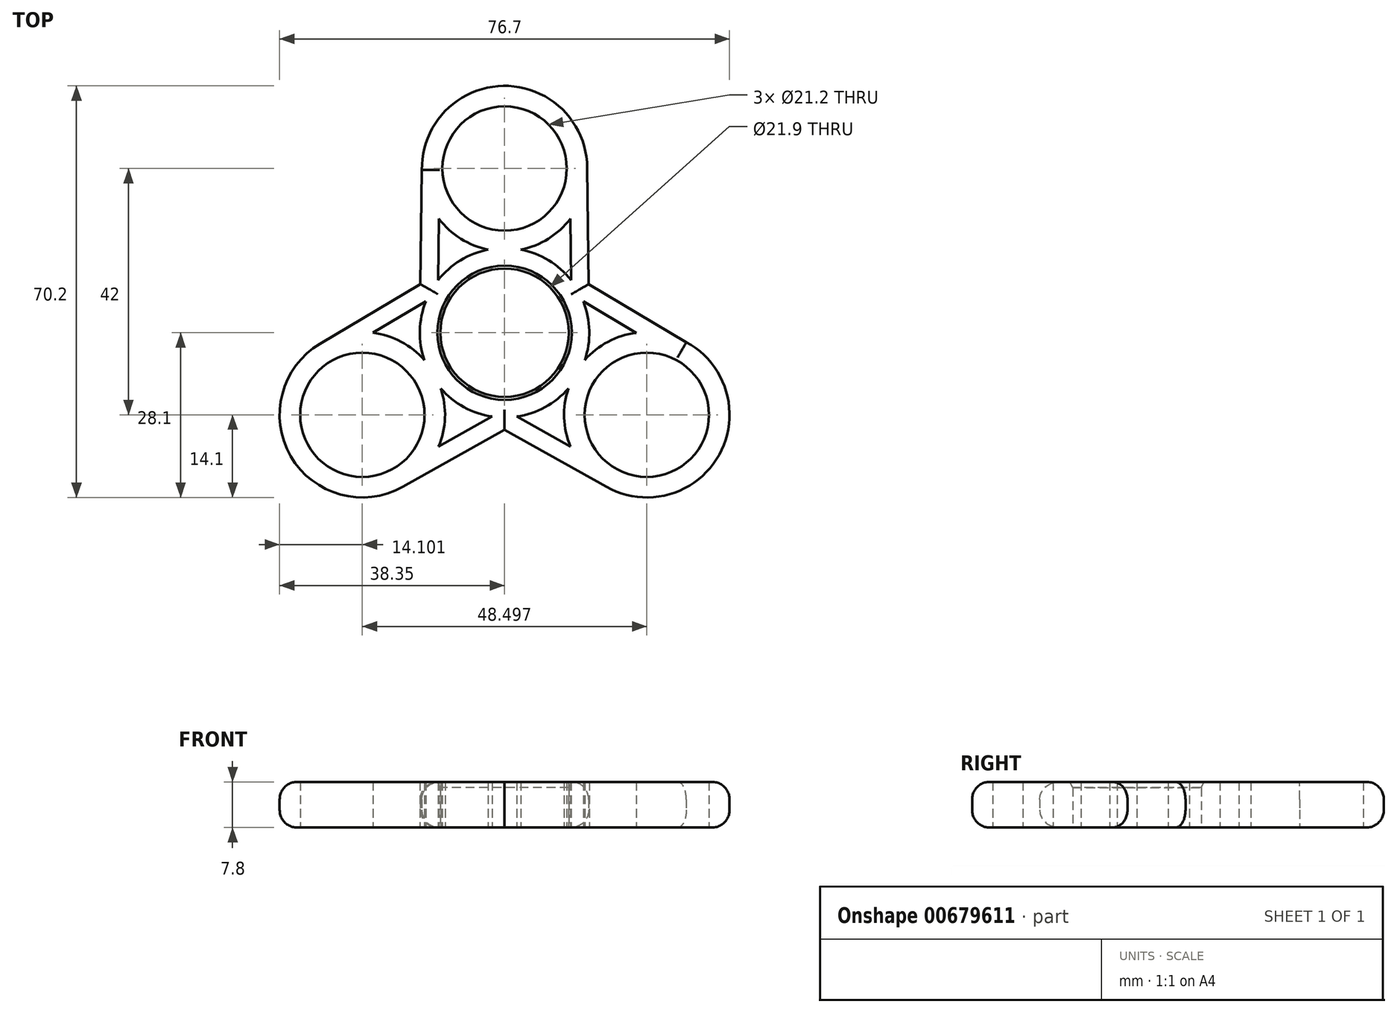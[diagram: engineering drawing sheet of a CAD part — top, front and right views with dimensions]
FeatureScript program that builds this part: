
annotation { "Feature Type Name" : "Feature", "Feature Type Description" : "" }
export const myFeature = defineFeature(function(context is Context, id is Id, definition is map)
    precondition{}
    {
        {
            var Q0;
            Q0=qCreatedBy(makeId("Top.planeOp"),FACE);
            var sketch = newSketch(context, id + "F0", { "sketchPlane" : qUnion([Q0])});
            skCircle(sketch, "E0", {"center": v(0, 0) * mm, "radius": 10.95 * mm});
            skCircle(sketch, "E1.0", {"center": v(0, 0) * mm, "radius": 14.45 * mm});
            skCircle(sketch, "E2.cCircle", {"center": v(0, 0) * mm, "radius": 14 * mm, "construction": true});
            skLineSegment(sketch, "E2.0", {"start": v(-24.25, -14) * mm, "end": v(0, 28) * mm, "construction": true});
            skLineSegment(sketch, "E2.1", {"start": v(0, 28) * mm, "end": v(24.25, -14) * mm, "construction": true});
            skLineSegment(sketch, "E2.2", {"start": v(24.25, -14) * mm, "end": v(-24.25, -14) * mm, "construction": true});
            skPoint(sketch, "E2.0.midPoint", {"position": v(-12.12, 7) * mm});
            skCircle(sketch, "E3", {"center": v(0, 28) * mm, "radius": 10.6 * mm});
            skCircle(sketch, "E4.0", {"center": v(0, 28) * mm, "radius": 14.1 * mm});
            skCircle(sketch, "E5", {"center": v(24.25, -14) * mm, "radius": 10.6 * mm});
            skCircle(sketch, "E6.0", {"center": v(24.25, -14) * mm, "radius": 14.1 * mm});
            skCircle(sketch, "E7", {"center": v(-24.25, -14) * mm, "radius": 10.6 * mm});
            skCircle(sketch, "E8.0", {"center": v(-24.25, -14) * mm, "radius": 14.1 * mm});
            skLineSegment(sketch, "E9", {"start": v(14.1, 28.18) * mm, "end": v(14.45, 0) * mm});
            skLineSegment(sketch, "E10", {"start": v(-14.1, 27.75) * mm, "end": v(-14.45, 0) * mm});
            skLineSegment(sketch, "E11.0", {"start": v(-11.1, 27.71) * mm, "end": v(-11.45, -0.04) * mm});
            skLineSegment(sketch, "E12.0", {"start": v(11.1, 28.14) * mm, "end": v(11.45, -0.04) * mm});
            skLineSegment(sketch, "E13", {"start": v(-31.45, -1.88) * mm, "end": v(-7.38, 12.42) * mm});
            skLineSegment(sketch, "E14", {"start": v(-17.35, -26.3) * mm, "end": v(7.07, -12.6) * mm});
            skLineSegment(sketch, "E15.0", {"start": v(-18.82, -23.68) * mm, "end": v(5.6, -9.99) * mm});
            skLineSegment(sketch, "E16.0", {"start": v(-29.92, -4.46) * mm, "end": v(-5.85, 9.84) * mm});
            skLineSegment(sketch, "E17", {"start": v(17.35, -26.3) * mm, "end": v(-7.07, -12.6) * mm});
            skLineSegment(sketch, "E18", {"start": v(30.97, -1.6) * mm, "end": v(7.39, 12.42) * mm});
            skLineSegment(sketch, "E19.0", {"start": v(29.44, -4.19) * mm, "end": v(5.85, 9.84) * mm});
            skLineSegment(sketch, "E20.0", {"start": v(18.82, -23.68) * mm, "end": v(-5.6, -9.99) * mm});
            skSolve(sketch);
        }
        {
            var Q0;
            Q0=qSketchRegion(id+"F0",true);
            var Q1;
            Q1=makeQuery(id+"F0.imprint","IMPRINT",FACE,{"disambiguationData":[TD([[makeQuery(id+"F0.imprint","IMPRINT",EDGE,{"derivedFrom":sQuery(id+"F0.wireOp",EDGE,"E0")}),-1.0]])]});
            var Q2;
            {var subQ0=sQuery(id+"F0.wireOp",EDGE,"E11.0");var subQ1=sQuery(id+"F0.wireOp",EDGE,"E1.0");var subQ2=makeQuery(id+"F0.imprint","INTERSECT",VERTEX,{"derivedFrom":[subQ1,subQ0]});Q2=makeQuery(id+"F0.imprint","IMPRINT",FACE,{"disambiguationData":[TD([[makeQuery(id+"F0.imprint","IMPRINT",EDGE,{"disambiguationData":[TD([[subQ2,-1.0]])],"derivedFrom":subQ1}),1.0]])]});}
            var Q3;
            {var subQ0=sQuery(id+"F0.wireOp",EDGE,"E15.0");var subQ1=sQuery(id+"F0.wireOp",EDGE,"E1.0");var subQ2=makeQuery(id+"F0.imprint","INTERSECT",VERTEX,{"derivedFrom":[subQ1,subQ0]});Q3=makeQuery(id+"F0.imprint","IMPRINT",FACE,{"disambiguationData":[TD([[makeQuery(id+"F0.imprint","IMPRINT",EDGE,{"disambiguationData":[TD([[subQ2,-1.0]])],"derivedFrom":subQ1}),1.0]])]});}
            var Q4;
            {var subQ0=sQuery(id+"F0.wireOp",EDGE,"E19.0");var subQ1=sQuery(id+"F0.wireOp",EDGE,"E1.0");var subQ2=makeQuery(id+"F0.imprint","INTERSECT",VERTEX,{"derivedFrom":[subQ1,subQ0]});Q4=makeQuery(id+"F0.imprint","IMPRINT",FACE,{"disambiguationData":[TD([[makeQuery(id+"F0.imprint","IMPRINT",EDGE,{"disambiguationData":[TD([[subQ2,-1.0]])],"derivedFrom":subQ1}),1.0]])]});}
            var Q5;
            {var subQ0=sQuery(id+"F0.wireOp",EDGE,"E6.0");var subQ1=sQuery(id+"F0.wireOp",EDGE,"E1.0");var subQ2=makeQuery(id+"F0.imprint","INTERSECT",VERTEX,{"disambiguationData":[OD(0.0)],"derivedFrom":[subQ1,subQ0]});Q5=makeQuery(id+"F0.imprint","IMPRINT",FACE,{"disambiguationData":[TD([[makeQuery(id+"F0.imprint","IMPRINT",EDGE,{"disambiguationData":[TD([[subQ2,-1.0]])],"derivedFrom":subQ1}),1.0]])]});}
            var Q6;
            {var subQ0=sQuery(id+"F0.wireOp",EDGE,"E4.0");var subQ1=sQuery(id+"F0.wireOp",EDGE,"E1.0");var subQ2=makeQuery(id+"F0.imprint","INTERSECT",VERTEX,{"disambiguationData":[OD(0.0)],"derivedFrom":[subQ1,subQ0]});Q6=makeQuery(id+"F0.imprint","IMPRINT",FACE,{"disambiguationData":[TD([[makeQuery(id+"F0.imprint","IMPRINT",EDGE,{"disambiguationData":[TD([[subQ2,-1.0]])],"derivedFrom":subQ1}),1.0]])]});}
            var Q7;
            {var subQ0=sQuery(id+"F0.wireOp",EDGE,"E8.0");var subQ1=sQuery(id+"F0.wireOp",EDGE,"E1.0");var subQ2=makeQuery(id+"F0.imprint","INTERSECT",VERTEX,{"disambiguationData":[OD(0.0)],"derivedFrom":[subQ1,subQ0]});Q7=makeQuery(id+"F0.imprint","IMPRINT",FACE,{"disambiguationData":[TD([[makeQuery(id+"F0.imprint","IMPRINT",EDGE,{"disambiguationData":[TD([[subQ2,-1.0]])],"derivedFrom":subQ1}),1.0]])]});}
            extrude(context, id + "F1", {"entities" : qUnion([Q0, Q1, Q2, Q3, Q4, Q5, Q6, Q7]), "depth" : 7.8 * mm, "offsetDistance" : 25 * mm});
        }
        {
            var Q0;
            {var subQ0=sQuery(id+"F0.wireOp",EDGE,"E8.0");Q0=makeQuery(id+"F1.opExtrude","CAP_EDGE",EDGE,{"disambiguationData":[OSD([subQ0]),TDD([makeQuery(id+"F0.imprint","IMPRINT",EDGE,{"disambiguationData":[TD([[makeQuery(id+"F0.imprint","INTERSECT",VERTEX,{"derivedFrom":[subQ0,sQuery(id+"F0.wireOp",EDGE,"E13")]}),-1.0]])],"derivedFrom":subQ0})])],"isStart":false});}
            var Q1;
            Q1=makeQuery(id+"F1.opExtrude","CAP_EDGE",EDGE,{"disambiguationData":[OSD([sQuery(id+"F0.wireOp",EDGE,"E17")])],"isStart":false});
            var Q2;
            Q2=makeQuery(id+"F1.opExtrude","CAP_EDGE",EDGE,{"disambiguationData":[OSD([sQuery(id+"F0.wireOp",EDGE,"E9")])],"isStart":false});
            var Q3;
            Q3=makeQuery(id+"F1.opExtrude","CAP_EDGE",EDGE,{"disambiguationData":[OSD([sQuery(id+"F0.wireOp",EDGE,"E17")])],"isStart":true});
            var Q4;
            Q4=makeQuery(id+"F1.opExtrude","CAP_EDGE",EDGE,{"disambiguationData":[OSD([sQuery(id+"F0.wireOp",EDGE,"E9")])],"isStart":true});
            var Q5;
            Q5=makeQuery(id+"F1.opExtrude","CAP_EDGE",EDGE,{"disambiguationData":[OSD([sQuery(id+"F0.wireOp",EDGE,"E13")])],"isStart":true});
            fillet(context, id + "F2", {"entities" : qUnion([Q0, Q1, Q2, Q3, Q4, Q5]), "radius" : 3 * mm, "tangentPropagation" : true, "allowEdgeOverflow" : false});
        }
        {
            var Q0;
            Q0=makeQuery(id+"F1.opExtrude","CAP_EDGE",EDGE,{"disambiguationData":[OSD([sQuery(id+"F0.wireOp",EDGE,"E0")])],"isStart":false});
            chamfer(context, id + "F3", {"entities" : qUnion([Q0]), "chamferType" : ChamferType.TWO_OFFSETS, "width1" : 1 * mm, "oppositeDirection" : false, "width2" : .5 * mm, "tangentPropagation" : true});
        }
    });
